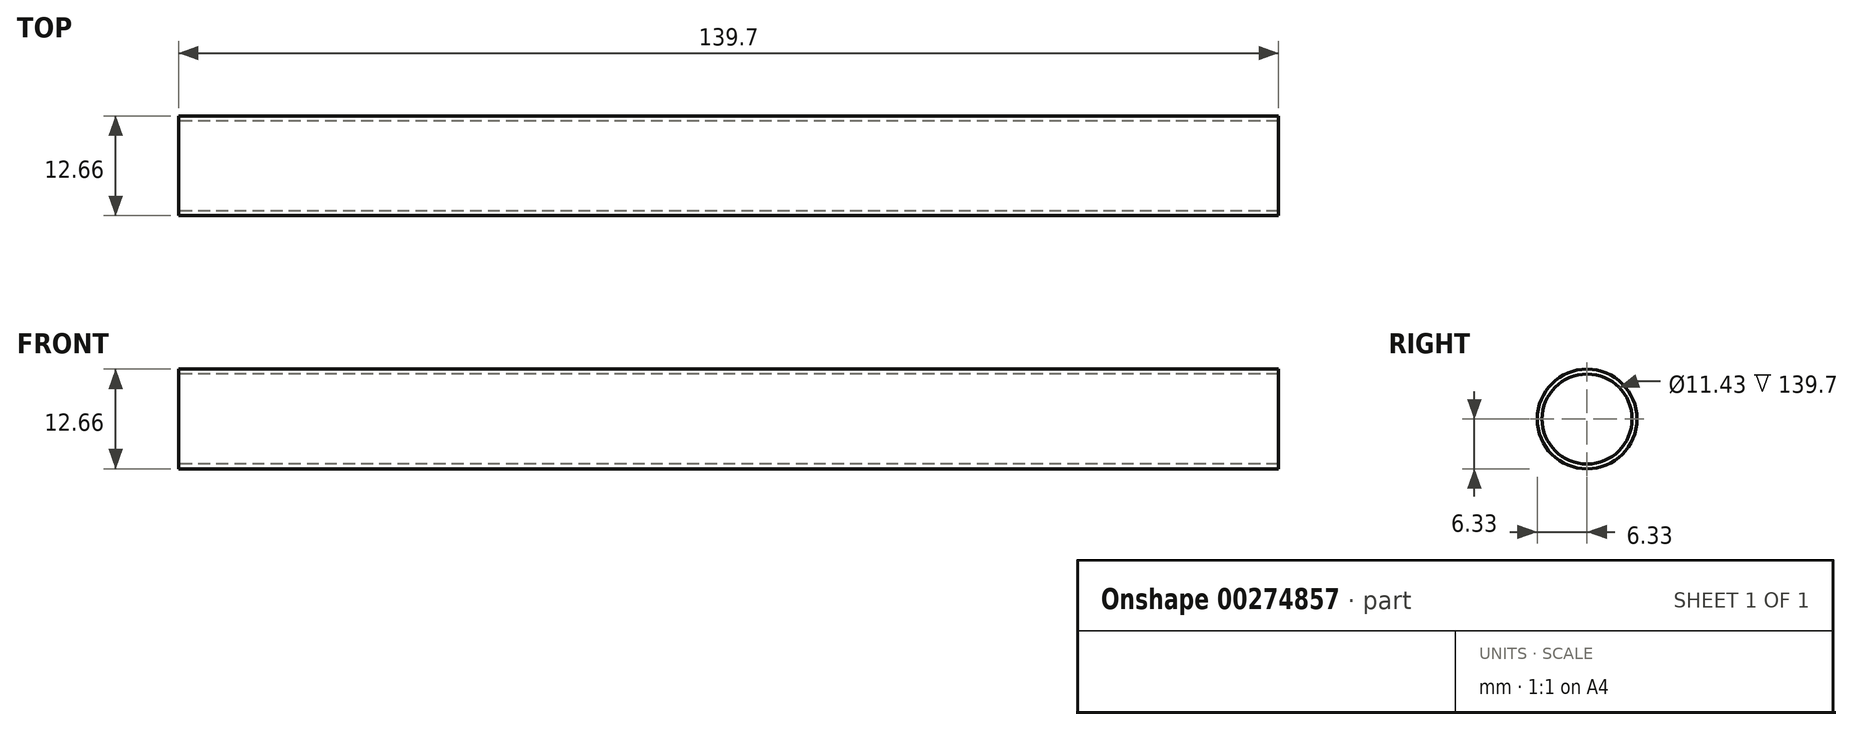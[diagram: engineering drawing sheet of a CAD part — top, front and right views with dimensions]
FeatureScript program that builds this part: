
annotation { "Feature Type Name" : "Feature", "Feature Type Description" : "" }
export const myFeature = defineFeature(function(context is Context, id is Id, definition is map)
    precondition{}
    {
        {
            var Q0;
            Q0=qCreatedBy(makeId("Right.planeOp"),FACE);
            var sketch = newSketch(context, id + "F0", { "sketchPlane" : qUnion([Q0])});
            skCircle(sketch, "E0", {"center": v(0, 0) * mm, "radius": 6.33 * mm});
            skSolve(sketch);
        }
        {
            var Q0;
            Q0=makeQuery(id+"F0.imprint","IMPRINT",FACE,{"disambiguationData":[TD([[makeQuery(id+"F0.imprint","IMPRINT",EDGE,{"derivedFrom":sQuery(id+"F0.wireOp",EDGE,"E0")}),1.0]])]});
            extrude(context, id + "F1", {"entities" : qUnion([Q0]), "depth" : 139.7 * mm});
        }
        {
            var Q0;
            Q0=makeQuery(id+"F1.opExtrude","CAP_FACE",FACE,{"disambiguationData":[OSD([sQuery(id+"F0.wireOp",EDGE,"E0")])],"isStart":false});
            var sketch = newSketch(context, id + "F2", { "sketchPlane" : qUnion([Q0])});
            skPoint(sketch, "E1", {"position": v(0, 0) * mm});
            skSolve(sketch);
        }
        {
            var Q0;
            Q0=sQuery(id+"F2.wireOp",VERTEX,"E1");
            var Q1;
            Q1=makeQuery(id+"F1.opExtrude","SWEPT_BODY",BODY,{"disambiguationData":[OSD([sQuery(id+"F0.wireOp",EDGE,"E0")])]});
            hole(context, id + "F3", {"style" : HoleStyle.SIMPLE, "endStyle" : HoleEndStyle.THROUGH, "holeDiameter" : 11.43 * mm, "tappedDepth" : 12.7 * mm, "tapClearance" : 3, "locations" : qUnion([Q0]), "scope" : qUnion([Q1]), "startStyle" : HoleStartStyle.SKETCH});
        }
    });
